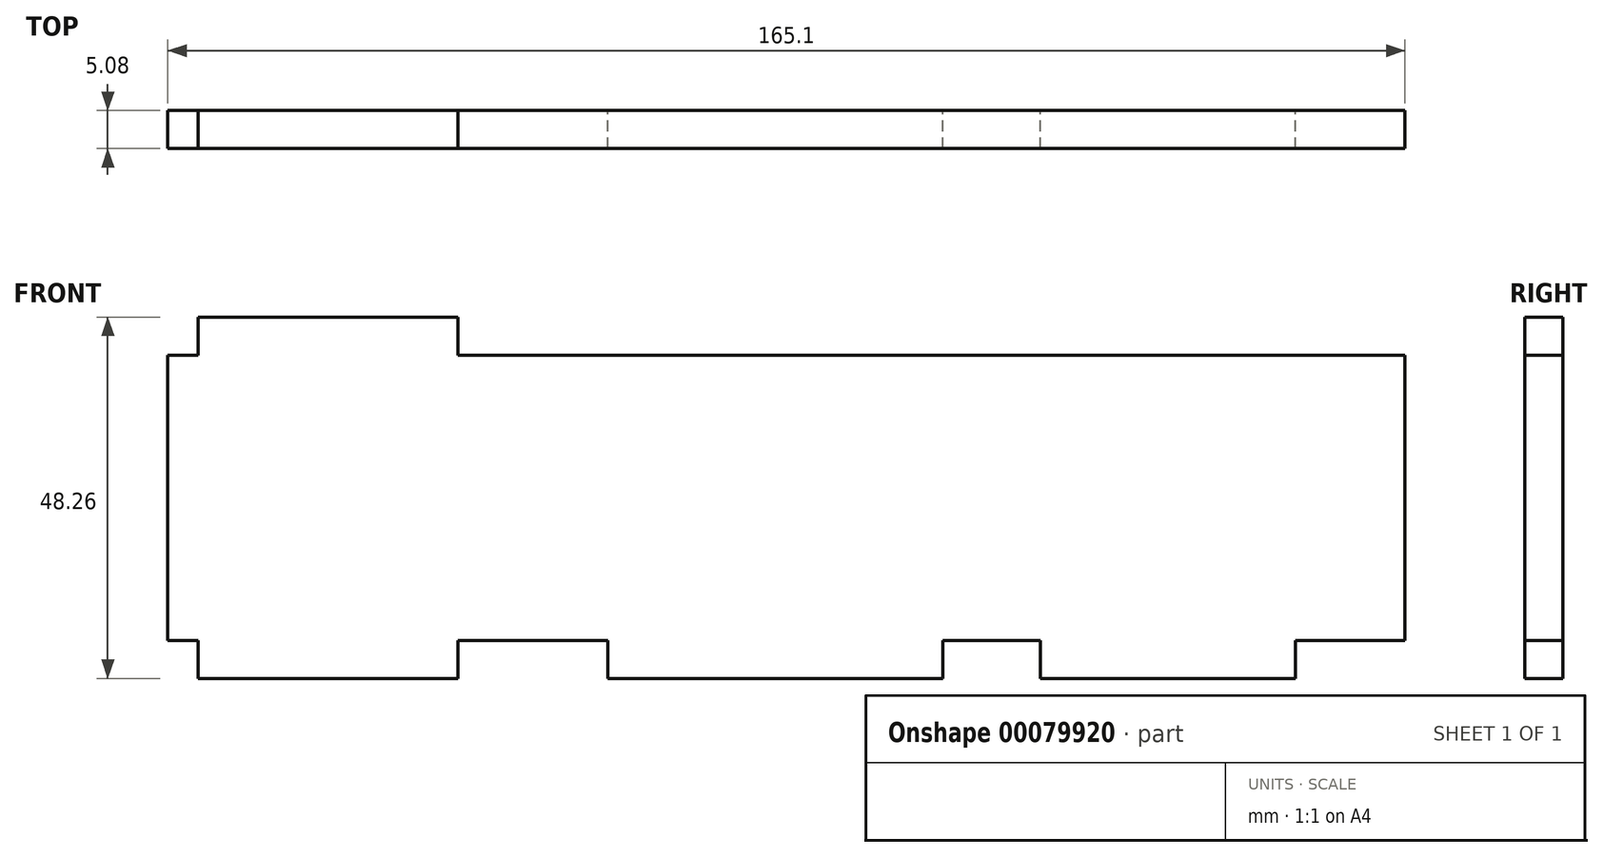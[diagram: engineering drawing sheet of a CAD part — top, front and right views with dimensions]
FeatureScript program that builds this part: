
annotation { "Feature Type Name" : "Feature", "Feature Type Description" : "" }
export const myFeature = defineFeature(function(context is Context, id is Id, definition is map)
    precondition{}
    {
        {
            var Q0;
            Q0=qCreatedBy(makeId("Front.planeOp"),FACE);
            var sketch = newSketch(context, id + "F0", { "sketchPlane" : qUnion([Q0])});
            skLineSegment(sketch, "E0.bottom", {"start": v(82.55, -19.05) * mm, "end": v(-82.55, -19.05) * mm});
            skLineSegment(sketch, "E0.top", {"start": v(82.55, 19.05) * mm, "end": v(-82.55, 19.05) * mm});
            skLineSegment(sketch, "E0.left", {"start": v(82.55, -19.05) * mm, "end": v(82.55, 19.05) * mm});
            skLineSegment(sketch, "E0.right", {"start": v(-82.55, -19.05) * mm, "end": v(-82.55, 19.05) * mm});
            skPoint(sketch, "E0.middle", {"position": v(0, 0) * mm});
            skLineSegment(sketch, "E1.bottom", {"start": v(-82.55, 19.05) * mm, "end": v(-60.55, 19.05) * mm});
            skLineSegment(sketch, "E1.left", {"start": v(-82.55, 19.05) * mm, "end": v(-82.55, 36.43) * mm});
            skLineSegment(sketch, "E2.bottom", {"start": v(-23.8, 19.05) * mm, "end": v(20.9, 19.05) * mm});
            skLineSegment(sketch, "E2.top", {"start": v(-23.8, 24.13) * mm, "end": v(20.9, 24.13) * mm});
            skLineSegment(sketch, "E2.left", {"start": v(-23.8, 19.05) * mm, "end": v(-23.8, 24.13) * mm});
            skLineSegment(sketch, "E2.right", {"start": v(20.9, 19.05) * mm, "end": v(20.9, 24.13) * mm});
            skLineSegment(sketch, "E3.bottom", {"start": v(33.9, 19.05) * mm, "end": v(67.9, 19.05) * mm});
            skLineSegment(sketch, "E3.top", {"start": v(33.9, 24.13) * mm, "end": v(67.9, 24.13) * mm});
            skLineSegment(sketch, "E3.left", {"start": v(33.9, 19.05) * mm, "end": v(33.9, 24.13) * mm});
            skLineSegment(sketch, "E3.right", {"start": v(67.9, 19.05) * mm, "end": v(67.9, 24.13) * mm});
            skLineSegment(sketch, "E4.bottom", {"start": v(-78.5, 19.05) * mm, "end": v(-43.8, 19.05) * mm});
            skLineSegment(sketch, "E4.top", {"start": v(-78.5, 24.13) * mm, "end": v(-43.8, 24.13) * mm});
            skLineSegment(sketch, "E4.left", {"start": v(-78.5, 19.05) * mm, "end": v(-78.5, 24.13) * mm});
            skLineSegment(sketch, "E4.right", {"start": v(-43.8, 19.05) * mm, "end": v(-43.8, 24.13) * mm});
            skLineSegment(sketch, "E5", {"start": v(82.55, -19.05) * mm, "end": v(82.55, 47.05) * mm, "construction": true});
            skLineSegment(sketch, "E6", {"start": v(-82.55, 0) * mm, "end": v(82.55, 0) * mm, "construction": true});
            skLineSegment(sketch, "E7.MirrorCS", {"start": v(-78.5, -24.13) * mm, "end": v(-43.8, -24.13) * mm});
            skLineSegment(sketch, "E8.MirrorCS", {"start": v(-43.8, -19.05) * mm, "end": v(-43.8, -24.13) * mm});
            skLineSegment(sketch, "E9.MirrorCS", {"start": v(-78.5, -19.05) * mm, "end": v(-78.5, -24.13) * mm});
            skLineSegment(sketch, "E10.MirrorCS", {"start": v(-23.8, -24.13) * mm, "end": v(20.9, -24.13) * mm});
            skLineSegment(sketch, "E11.MirrorCS", {"start": v(-23.8, -19.05) * mm, "end": v(-23.8, -24.13) * mm});
            skLineSegment(sketch, "E12.MirrorCS", {"start": v(20.9, -19.05) * mm, "end": v(20.9, -24.13) * mm});
            skLineSegment(sketch, "E13.MirrorCS", {"start": v(33.9, -19.05) * mm, "end": v(33.9, -24.13) * mm});
            skLineSegment(sketch, "E14.MirrorCS", {"start": v(33.9, -24.13) * mm, "end": v(67.9, -24.13) * mm});
            skLineSegment(sketch, "E15.MirrorCS", {"start": v(67.9, -19.05) * mm, "end": v(67.9, -24.13) * mm});
            skSolve(sketch);
        }
        {
            var Q0;
            Q0=makeQuery(id+"F0.imprint","IMPRINT",FACE,{"disambiguationData":[TD([[makeQuery(id+"F0.imprint","IMPRINT",EDGE,{"derivedFrom":sQuery(id+"F0.wireOp",EDGE,"E0.bottom")}),-1.0]])]});
            var Q1;
            Q1=makeQuery(id+"F0.imprint","IMPRINT",FACE,{"disambiguationData":[TD([[makeQuery(id+"F0.imprint","IMPRINT",EDGE,{"derivedFrom":sQuery(id+"F0.wireOp",EDGE,"E4.top")}),-1.0]])]});
            var Q2;
            Q2=makeQuery(id+"F0.imprint","IMPRINT",FACE,{"disambiguationData":[TD([[makeQuery(id+"F0.imprint","IMPRINT",EDGE,{"derivedFrom":sQuery(id+"F0.wireOp",EDGE,"E2.bottom")}),1.0]])]});
            var Q3;
            Q3=makeQuery(id+"F0.imprint","IMPRINT",FACE,{"disambiguationData":[TD([[makeQuery(id+"F0.imprint","IMPRINT",EDGE,{"derivedFrom":sQuery(id+"F0.wireOp",EDGE,"E3.bottom")}),1.0]])]});
            var Q4;
            Q4=makeQuery(id+"F0.imprint","IMPRINT",FACE,{"disambiguationData":[TD([[makeQuery(id+"F0.imprint","IMPRINT",EDGE,{"derivedFrom":sQuery(id+"F0.wireOp",EDGE,"E7.MirrorCS")}),1.0]])]});
            var Q5;
            Q5=makeQuery(id+"F0.imprint","IMPRINT",FACE,{"disambiguationData":[TD([[makeQuery(id+"F0.imprint","IMPRINT",EDGE,{"derivedFrom":sQuery(id+"F0.wireOp",EDGE,"E10.MirrorCS")}),1.0]])]});
            var Q6;
            {var subQ0=sQuery(id+"F0.wireOp",EDGE,"E13.MirrorCS");Q6=makeQuery(id+"F0.imprint","IMPRINT",FACE,{"disambiguationData":[TD([[makeQuery(id+"F0.imprint","IMPRINT",EDGE,{"derivedFrom":subQ0}),1.0]])]});}
            extrude(context, id + "F1", {"entities" : qUnion([Q0, Q1, Q2, Q3, Q4, Q5, Q6]), "depth" : 5.08 * mm});
        }
    });
